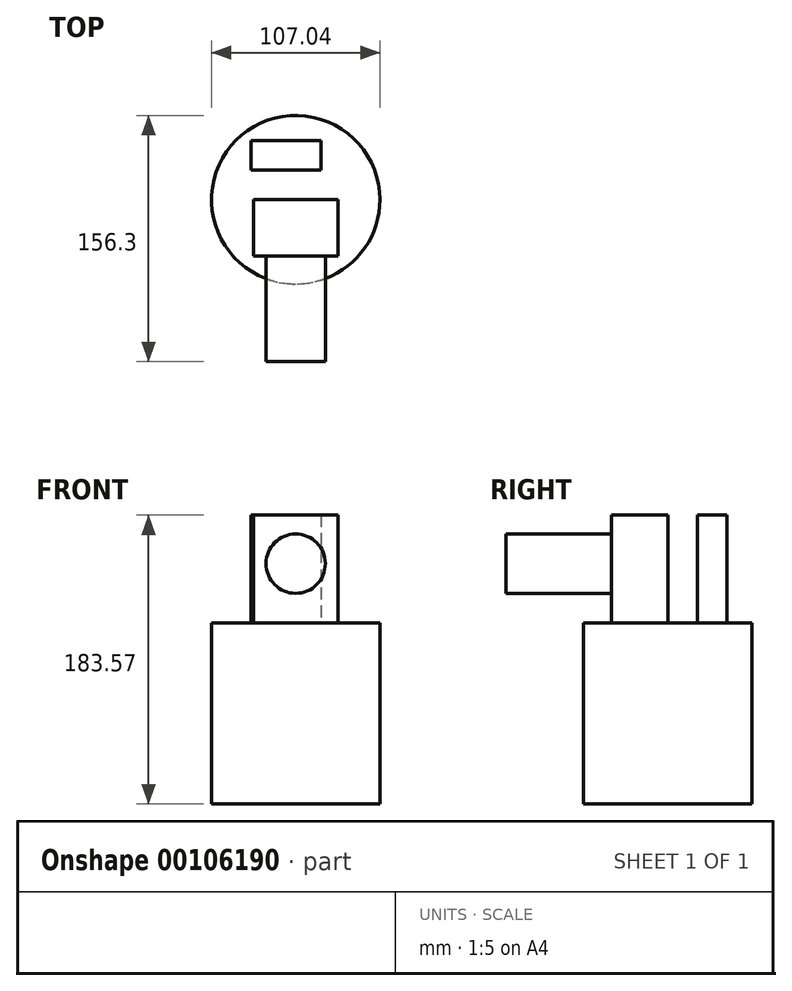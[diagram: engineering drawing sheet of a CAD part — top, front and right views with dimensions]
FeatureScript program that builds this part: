
annotation { "Feature Type Name" : "Feature", "Feature Type Description" : "" }
export const myFeature = defineFeature(function(context is Context, id is Id, definition is map)
    precondition{}
    {
        {
            var Q0;
            Q0=qCreatedBy(makeId("Top.planeOp"),FACE);
            var sketch = newSketch(context, id + "F0", { "sketchPlane" : qUnion([Q0])});
            skCircle(sketch, "E0", {"center": v(0, 0) * mm, "radius": 53.52 * mm});
            skSolve(sketch);
        }
        {
            var Q0;
            Q0 = qSketchRegion(id + "F0", true);
            extrude(context, id + "F1", {"entities" : qUnion([Q0]), "depth" : 115.16 * mm});
        }
        {
            var Q0;
            Q0=makeQuery(id+"F1.opExtrude","CAP_FACE",FACE,{"disambiguationData":[OSD([sQuery(id+"F0.wireOp",EDGE,"E0")])],"isStart":false});
            var sketch = newSketch(context, id + "F2", { "sketchPlane" : qUnion([Q0])});
            skLineSegment(sketch, "E1.bottom", {"start": v(-28.38, 18.84) * mm, "end": v(16.24, 18.84) * mm});
            skLineSegment(sketch, "E1.top", {"start": v(-28.38, 37.67) * mm, "end": v(16.24, 37.67) * mm});
            skLineSegment(sketch, "E1.left", {"start": v(-28.38, 18.84) * mm, "end": v(-28.38, 37.67) * mm});
            skLineSegment(sketch, "E1.right", {"start": v(16.24, 18.84) * mm, "end": v(16.24, 37.67) * mm});
            skLineSegment(sketch, "E2.bottom", {"start": v(26.78, 0) * mm, "end": v(-26.78, 0) * mm});
            skLineSegment(sketch, "E2.top", {"start": v(26.78, -35.87) * mm, "end": v(-26.78, -35.87) * mm});
            skLineSegment(sketch, "E2.left", {"start": v(26.78, 0) * mm, "end": v(26.78, -35.87) * mm});
            skLineSegment(sketch, "E2.right", {"start": v(-26.78, 0) * mm, "end": v(-26.78, -35.87) * mm});
            skPoint(sketch, "E2.middle", {"position": v(0, -17.93) * mm});
            skSolve(sketch);
        }
        {
            var Q0;
            Q0 = qSketchRegion(id + "F2", true);
            extrude(context, id + "F3", {"entities" : qUnion([Q0]), "operationType" : NewBodyOperationType.ADD, "depth" : 68.4 * mm});
        }
        {
            var Q0;
            Q0=makeQuery(id+"F3.opExtrude","SWEPT_FACE",FACE,{"disambiguationData":[OSD([sQuery(id+"F2.wireOp",EDGE,"E2.top")])]});
            var sketch = newSketch(context, id + "F4", { "sketchPlane" : qUnion([Q0])});
            skCircle(sketch, "E3", {"center": v(0, 152.68) * mm, "radius": 18.84 * mm});
            skSolve(sketch);
        }
        {
            var Q0;
            Q0 = qSketchRegion(id + "F4", true);
            extrude(context, id + "F5", {"entities" : qUnion([Q0]), "operationType" : NewBodyOperationType.ADD, "depth" : 66.9 * mm});
        }
    });
